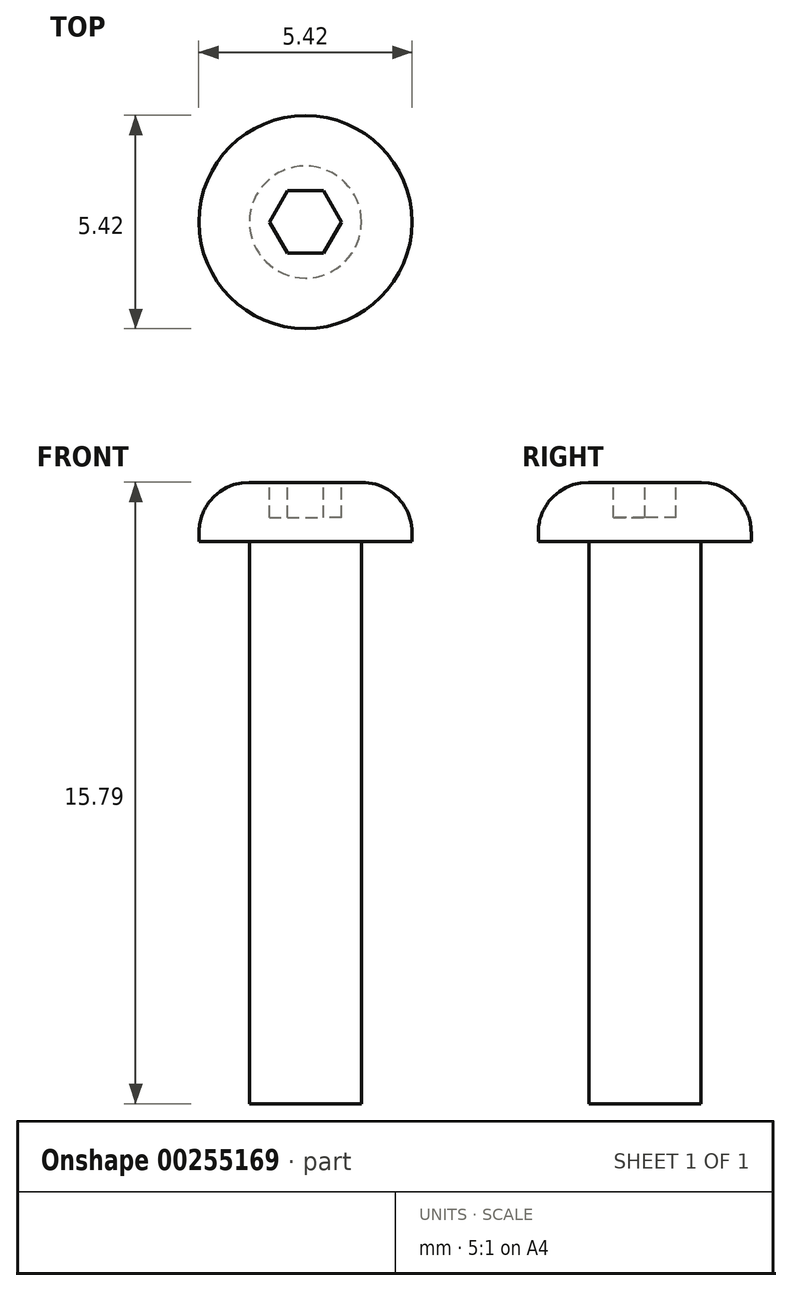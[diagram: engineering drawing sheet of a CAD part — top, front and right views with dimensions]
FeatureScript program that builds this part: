
annotation { "Feature Type Name" : "Feature", "Feature Type Description" : "" }
export const myFeature = defineFeature(function(context is Context, id is Id, definition is map)
    precondition{}
    {
        {
            var Q0;
            Q0=qCreatedBy(makeId("Top.planeOp"),FACE);
            var sketch = newSketch(context, id + "F0", { "sketchPlane" : qUnion([Q0])});
            skCircle(sketch, "E0", {"center": v(0, 0) * mm, "radius": 1.42 * mm});
            skSolve(sketch);
        }
        {
            var Q0;
            Q0=qSketchRegion(id+"F0",true);
            extrude(context, id + "F1", {"entities" : qUnion([Q0]), "depth" : 14.29 * mm});
        }
        {
            var Q0;
            Q0=makeQuery(id+"F1.opExtrude","CAP_FACE",FACE,{"disambiguationData":[OSD([sQuery(id+"F0.wireOp",EDGE,"E0")])],"isStart":false});
            var sketch = newSketch(context, id + "F2", { "sketchPlane" : qUnion([Q0])});
            skCircle(sketch, "E1", {"center": v(0, 0) * mm, "radius": 2.7 * mm});
            skSolve(sketch);
        }
        {
            var Q0;
            Q0=qSketchRegion(id+"F2",true);
            extrude(context, id + "F3", {"entities" : qUnion([Q0]), "operationType" : NewBodyOperationType.ADD, "depth" : 1.5 * mm});
        }
        {
            var Q0;
            Q0=makeQuery(id+"F3.opExtrude","CAP_EDGE",EDGE,{"disambiguationData":[OSD([sQuery(id+"F2.wireOp",EDGE,"E1")])],"isStart":false});
            fillet(context, id + "F4", {"entities" : qUnion([Q0]), "radius" : 1.27 * mm, "tangentPropagation" : true, "allowEdgeOverflow" : false});
        }
        {
            var Q0;
            Q0=makeQuery(id+"F3.opExtrude","CAP_FACE",FACE,{"disambiguationData":[OSD([sQuery(id+"F2.wireOp",EDGE,"E1")])],"isStart":false});
            var sketch = newSketch(context, id + "F5", { "sketchPlane" : qUnion([Q0])});
            skCircle(sketch, "E2.cCircle", {"center": v(0, 0) * mm, "radius": 0.8 * mm, "construction": true});
            skLineSegment(sketch, "E2.0", {"start": v(0.92, 0) * mm, "end": v(0.46, -0.8) * mm});
            skLineSegment(sketch, "E2.1", {"start": v(0.46, -0.8) * mm, "end": v(-0.46, -0.8) * mm});
            skLineSegment(sketch, "E2.2", {"start": v(-0.46, -0.8) * mm, "end": v(-0.92, 0) * mm});
            skLineSegment(sketch, "E2.3", {"start": v(-0.92, 0) * mm, "end": v(-0.46, 0.8) * mm});
            skLineSegment(sketch, "E2.4", {"start": v(-0.46, 0.8) * mm, "end": v(0.46, 0.8) * mm});
            skLineSegment(sketch, "E2.5", {"start": v(0.46, 0.8) * mm, "end": v(0.92, 0) * mm});
            skPoint(sketch, "E2.0.midPoint", {"position": v(0.69, -0.4) * mm});
            skSolve(sketch);
        }
        {
            var Q0;
            Q0=qSketchRegion(id+"F5",true);
            extrude(context, id + "F6", {"entities" : qUnion([Q0]), "operationType" : NewBodyOperationType.REMOVE, "oppositeDirection" : true, "depth" : 0.9 * mm});
        }
    });
